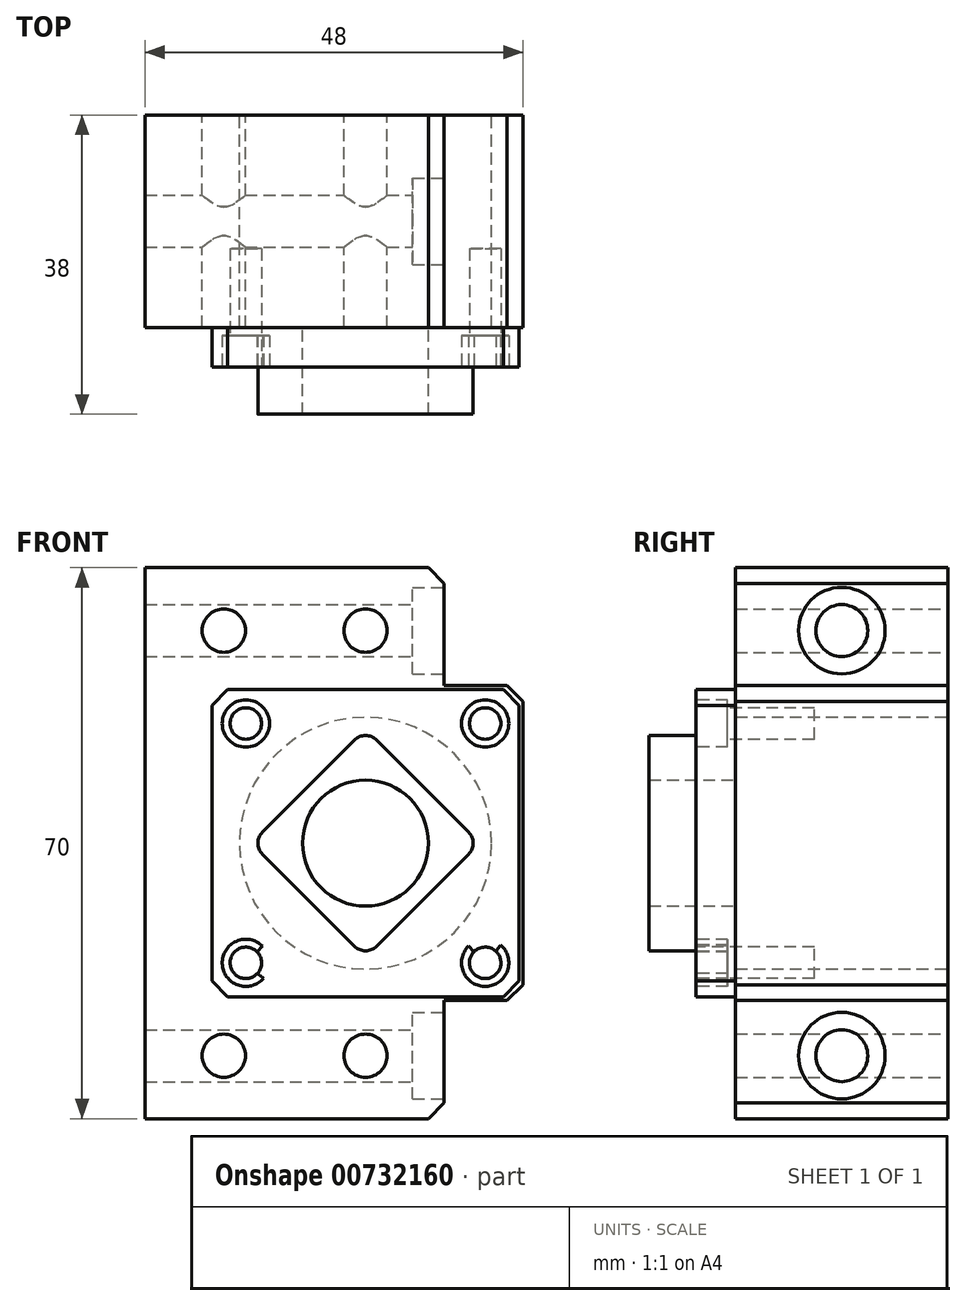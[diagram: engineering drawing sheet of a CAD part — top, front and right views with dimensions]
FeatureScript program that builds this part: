
annotation { "Feature Type Name" : "Feature", "Feature Type Description" : "" }
export const myFeature = defineFeature(function(context is Context, id is Id, definition is map)
    precondition{}
    {
        {
            var Q0;
            Q0=qCreatedBy(makeId("Front.planeOp"),FACE);
            var sketch = newSketch(context, id + "F0", { "sketchPlane" : qUnion([Q0])});
            skLineSegment(sketch, "E0.bottom", {"start": v(0, 0) * mm, "end": v(38, 0) * mm});
            skLineSegment(sketch, "E0.top", {"start": v(0, 70) * mm, "end": v(38, 70) * mm});
            skLineSegment(sketch, "E0.left", {"start": v(0, 0) * mm, "end": v(0, 70) * mm});
            skLineSegment(sketch, "E0.right", {"start": v(48, 15) * mm, "end": v(48, 55) * mm});
            skCircle(sketch, "E1", {"center": v(28, 35) * mm, "radius": 16 * mm});
            skCircle(sketch, "E2", {"center": v(10, 62) * mm, "radius": 2.75 * mm});
            skCircle(sketch, "E3", {"center": v(28, 62) * mm, "radius": 2.75 * mm});
            skCircle(sketch, "E4", {"center": v(10, 8) * mm, "radius": 2.75 * mm});
            skCircle(sketch, "E5", {"center": v(28, 8) * mm, "radius": 2.75 * mm});
            skLineSegment(sketch, "E6.top", {"start": v(48, 55) * mm, "end": v(38, 55) * mm});
            skLineSegment(sketch, "E6.right", {"start": v(38, 70) * mm, "end": v(38, 55) * mm});
            skLineSegment(sketch, "E7.top", {"start": v(48, 15) * mm, "end": v(38, 15) * mm});
            skLineSegment(sketch, "E7.right", {"start": v(38, 0) * mm, "end": v(38, 15) * mm});
            skPoint(sketch, "E6.bottom.start.orphan", {"position": v(48, 70) * mm});
            skSolve(sketch);
        }
        {
            var Q0;
            Q0=makeQuery(id+"F0.imprint","IMPRINT",FACE,{"disambiguationData":[TD([[makeQuery(id+"F0.imprint","IMPRINT",EDGE,{"derivedFrom":sQuery(id+"F0.wireOp",EDGE,"E0.bottom")}),1.0]])]});
            extrude(context, id + "F1", {"entities" : qUnion([Q0]), "depth" : 27 * mm, "offsetDistance" : 25 * mm});
        }
        {
            var Q0;
            Q0=makeQuery(id+"F1.opExtrude","SWEPT_FACE",FACE,{"disambiguationData":[OSD([sQuery(id+"F0.wireOp",EDGE,"E6.right")])]});
            var sketch = newSketch(context, id + "F2", { "sketchPlane" : qUnion([Q0])});
            skCircle(sketch, "E8", {"center": v(-13.5, 62) * mm, "radius": 3.3 * mm});
            skPoint(sketch, "E8.centerSnap0", {"position": v(-22.98, 62) * mm});
            skCircle(sketch, "E9", {"center": v(-13.5, 8) * mm, "radius": 3.3 * mm});
            skSolve(sketch);
        }
        {
            var Q0;
            Q0=qSketchRegion(id+"F2",true);
            extrude(context, id + "F3", {"entities" : qUnion([Q0]), "operationType" : NewBodyOperationType.REMOVE, "oppositeDirection" : true, "depth" : 38 * mm, "offsetDistance" : 25 * mm});
        }
        {
            var Q0;
            Q0=makeQuery(id+"F1.opExtrude","SWEPT_FACE",FACE,{"disambiguationData":[OSD([sQuery(id+"F0.wireOp",EDGE,"E6.right")])]});
            var sketch = newSketch(context, id + "F4", { "sketchPlane" : qUnion([Q0])});
            skCircle(sketch, "E10", {"center": v(-13.5, 62) * mm, "radius": 5.5 * mm});
            skCircle(sketch, "E11", {"center": v(-13.5, 8) * mm, "radius": 5.5 * mm});
            skSolve(sketch);
        }
        {
            var Q0;
            Q0=qSketchRegion(id+"F4",true);
            extrude(context, id + "F5", {"entities" : qUnion([Q0]), "operationType" : NewBodyOperationType.REMOVE, "oppositeDirection" : true, "depth" : 4 * mm, "offsetDistance" : 25 * mm});
        }
        {
            var Q0;
            Q0=makeQuery(id+"F1.opExtrude","SWEPT_EDGE",EDGE,{"disambiguationData":[OSD([sQuery(id+"F0.wireOp",EDGE,"E0.top"),sQuery(id+"F0.wireOp",EDGE,"E6.right")])]});
            var Q1;
            Q1=makeQuery(id+"F1.opExtrude","SWEPT_EDGE",EDGE,{"disambiguationData":[OSD([sQuery(id+"F0.wireOp",EDGE,"E0.right"),sQuery(id+"F0.wireOp",EDGE,"E6.top")])]});
            var Q2;
            Q2=makeQuery(id+"F1.opExtrude","SWEPT_EDGE",EDGE,{"disambiguationData":[OSD([sQuery(id+"F0.wireOp",EDGE,"E0.bottom"),sQuery(id+"F0.wireOp",EDGE,"E7.right")])]});
            var Q3;
            Q3=makeQuery(id+"F1.opExtrude","SWEPT_EDGE",EDGE,{"disambiguationData":[OSD([sQuery(id+"F0.wireOp",EDGE,"E0.right"),sQuery(id+"F0.wireOp",EDGE,"E7.top")])]});
            chamfer(context, id + "F6", {"entities" : qUnion([Q0, Q1, Q2, Q3]), "width" : 2 * mm, "tangentPropagation" : true});
        }
        {
            var Q0;
            Q0=makeQuery(id+"F1.opExtrude","CAP_FACE",FACE,{"disambiguationData":[OSD([sQuery(id+"F0.wireOp",EDGE,"E0.bottom"),sQuery(id+"F0.wireOp",EDGE,"E0.top"),sQuery(id+"F0.wireOp",EDGE,"E0.left"),sQuery(id+"F0.wireOp",EDGE,"E0.right"),sQuery(id+"F0.wireOp",EDGE,"E1"),sQuery(id+"F0.wireOp",EDGE,"E2"),sQuery(id+"F0.wireOp",EDGE,"E3"),sQuery(id+"F0.wireOp",EDGE,"E4"),sQuery(id+"F0.wireOp",EDGE,"E5"),sQuery(id+"F0.wireOp",EDGE,"E6.top"),sQuery(id+"F0.wireOp",EDGE,"E6.right"),sQuery(id+"F0.wireOp",EDGE,"E7.top"),sQuery(id+"F0.wireOp",EDGE,"E7.right")])],"isStart":false});
            var sketch = newSketch(context, id + "F7", { "sketchPlane" : qUnion([Q0])});
            skLineSegment(sketch, "E12.bottom", {"start": v(8.5, 15.5) * mm, "end": v(47.5, 15.5) * mm});
            skLineSegment(sketch, "E12.top", {"start": v(8.5, 54.5) * mm, "end": v(47.5, 54.5) * mm});
            skLineSegment(sketch, "E12.left", {"start": v(8.5, 15.5) * mm, "end": v(8.5, 54.5) * mm});
            skLineSegment(sketch, "E12.right", {"start": v(47.5, 15.5) * mm, "end": v(47.5, 54.5) * mm});
            skCircle(sketch, "E13", {"center": v(28, 35) * mm, "radius": 8 * mm});
            skSolve(sketch);
        }
        {
            var Q0;
            {var subQ11=sQuery(id+"F7.wireOp",EDGE,"E12.left");Q0=makeQuery(id+"F7.imprint","IMPRINT",FACE,{"disambiguationData":[TD([[makeQuery(id+"F7.imprint","IMPRINT",EDGE,{"derivedFrom":subQ11}),-1.0]])]});}
            var Q1;
            {var subQ0=sQuery(id+"F7.wireOp",EDGE,"E12.right");var subQ1=sQuery(id+"F7.wireOp",EDGE,"E12.top");var subQ2=makeQuery(id+"F7.imprint","INTERSECT",VERTEX,{"derivedFrom":[subQ1,subQ0]});Q1=makeQuery(id+"F7.imprint","IMPRINT",FACE,{"disambiguationData":[TD([[makeQuery(id+"F7.imprint","IMPRINT",EDGE,{"disambiguationData":[TD([[subQ2,1.0]])],"derivedFrom":subQ1}),-1.0]])]});}
            var Q2;
            {var subQ0=sQuery(id+"F7.wireOp",EDGE,"E12.right");var subQ1=sQuery(id+"F7.wireOp",EDGE,"E12.bottom");var subQ2=makeQuery(id+"F7.imprint","INTERSECT",VERTEX,{"derivedFrom":[subQ1,subQ0]});Q2=makeQuery(id+"F7.imprint","IMPRINT",FACE,{"disambiguationData":[TD([[makeQuery(id+"F7.imprint","IMPRINT",EDGE,{"disambiguationData":[TD([[subQ2,1.0]])],"derivedFrom":subQ1}),1.0]])]});}
            var Q3;
            Q3=makeQuery(id+"F7.imprint","IMPRINT",FACE,{"disambiguationData":[TD([[makeQuery(id+"F7.imprint","IMPRINT",EDGE,{"derivedFrom":sQuery(id+"F7.wireOp",EDGE,"E13")}),-1.0]])]});
            extrude(context, id + "F8", {"entities" : qUnion([Q0, Q1, Q2, Q3]), "operationType" : NewBodyOperationType.ADD, "depth" : 5 * mm, "offsetDistance" : 25 * mm});
        }
        {
            var Q0;
            Q0=makeQuery(id+"F8.opExtrude","SWEPT_EDGE",EDGE,{"disambiguationData":[OSD([sQuery(id+"F7.wireOp",EDGE,"E12.bottom"),sQuery(id+"F7.wireOp",EDGE,"E12.left")])]});
            var Q1;
            Q1=makeQuery(id+"F8.opExtrude","SWEPT_EDGE",EDGE,{"disambiguationData":[OSD([sQuery(id+"F7.wireOp",EDGE,"E12.bottom"),sQuery(id+"F7.wireOp",EDGE,"E12.right")])]});
            var Q2;
            Q2=makeQuery(id+"F8.opExtrude","SWEPT_EDGE",EDGE,{"disambiguationData":[OSD([sQuery(id+"F7.wireOp",EDGE,"E12.top"),sQuery(id+"F7.wireOp",EDGE,"E12.left")])]});
            var Q3;
            Q3=makeQuery(id+"F8.opExtrude","SWEPT_EDGE",EDGE,{"disambiguationData":[OSD([sQuery(id+"F7.wireOp",EDGE,"E12.top"),sQuery(id+"F7.wireOp",EDGE,"E12.right")])]});
            chamfer(context, id + "F9", {"entities" : qUnion([Q0, Q1, Q2, Q3]), "width" : 2 * mm, "tangentPropagation" : true});
        }
        {
            var Q0;
            Q0=makeQuery(id+"F8.opExtrude","CAP_FACE",FACE,{"disambiguationData":[OSD([sQuery(id+"F7.wireOp",EDGE,"E12.bottom"),sQuery(id+"F7.wireOp",EDGE,"E12.top"),sQuery(id+"F7.wireOp",EDGE,"E12.left"),sQuery(id+"F7.wireOp",EDGE,"E12.right"),sQuery(id+"F7.wireOp",EDGE,"E13")])],"isStart":false});
            var sketch = newSketch(context, id + "F10", { "sketchPlane" : qUnion([Q0])});
            skCircle(sketch, "E14", {"center": v(28, 35) * mm, "radius": 21.5 * mm});
            skLineSegment(sketch, "E15", {"start": v(28, 35) * mm, "end": v(46.5, 53.5) * mm});
            skLineSegment(sketch, "E16", {"start": v(28, 35) * mm, "end": v(9.5, 16.5) * mm});
            skLineSegment(sketch, "E17", {"start": v(9.5, 16.5) * mm, "end": v(28, 35) * mm});
            skLineSegment(sketch, "E18", {"start": v(28, 35) * mm, "end": v(46.5, 16.5) * mm});
            skLineSegment(sketch, "E19", {"start": v(46.5, 16.5) * mm, "end": v(28, 35) * mm});
            skLineSegment(sketch, "E20", {"start": v(28, 35) * mm, "end": v(9.5, 53.5) * mm});
            skCircle(sketch, "E21", {"center": v(43.2, 50.2) * mm, "radius": 3 * mm});
            skCircle(sketch, "E22", {"center": v(43.2, 19.8) * mm, "radius": 3 * mm});
            skCircle(sketch, "E23", {"center": v(12.8, 19.8) * mm, "radius": 3 * mm});
            skCircle(sketch, "E24", {"center": v(12.8, 50.2) * mm, "radius": 3 * mm});
            skSolve(sketch);
        }
        {
            var Q0;
            {var subQ0=sQuery(id+"F10.wireOp",EDGE,"E15");var subQ1=sQuery(id+"F10.wireOp",EDGE,"E14");var subQ2=makeQuery(id+"F10.imprint","INTERSECT",VERTEX,{"derivedFrom":[subQ1,subQ0]});Q0=makeQuery(id+"F10.imprint","IMPRINT",FACE,{"disambiguationData":[TD([[makeQuery(id+"F10.imprint","IMPRINT",EDGE,{"disambiguationData":[TD([[subQ2,-1.0]])],"derivedFrom":subQ1}),-1.0]])]});}
            var Q1;
            {var subQ0=sQuery(id+"F10.wireOp",EDGE,"E15");var subQ1=sQuery(id+"F10.wireOp",EDGE,"E14");var subQ2=makeQuery(id+"F10.imprint","INTERSECT",VERTEX,{"derivedFrom":[subQ1,subQ0]});Q1=makeQuery(id+"F10.imprint","IMPRINT",FACE,{"disambiguationData":[TD([[makeQuery(id+"F10.imprint","IMPRINT",EDGE,{"disambiguationData":[TD([[subQ2,1.0]])],"derivedFrom":subQ1}),1.0]])]});}
            var Q2;
            {var subQ0=sQuery(id+"F10.wireOp",EDGE,"E15");var subQ1=sQuery(id+"F10.wireOp",EDGE,"E14");var subQ2=makeQuery(id+"F10.imprint","INTERSECT",VERTEX,{"derivedFrom":[subQ1,subQ0]});Q2=makeQuery(id+"F10.imprint","IMPRINT",FACE,{"disambiguationData":[TD([[makeQuery(id+"F10.imprint","IMPRINT",EDGE,{"disambiguationData":[TD([[subQ2,1.0]])],"derivedFrom":subQ1}),-1.0]])]});}
            var Q3;
            {var subQ0=sQuery(id+"F10.wireOp",EDGE,"E15");var subQ1=sQuery(id+"F10.wireOp",EDGE,"E14");var subQ2=makeQuery(id+"F10.imprint","INTERSECT",VERTEX,{"derivedFrom":[subQ1,subQ0]});Q3=makeQuery(id+"F10.imprint","IMPRINT",FACE,{"disambiguationData":[TD([[makeQuery(id+"F10.imprint","IMPRINT",EDGE,{"disambiguationData":[TD([[subQ2,-1.0]])],"derivedFrom":subQ1}),1.0]])]});}
            var Q4;
            {var subQ0=sQuery(id+"F10.wireOp",EDGE,"E19");var subQ1=sQuery(id+"F10.wireOp",EDGE,"E14");var subQ2=makeQuery(id+"F10.imprint","INTERSECT",VERTEX,{"derivedFrom":[subQ1,subQ0]});Q4=makeQuery(id+"F10.imprint","IMPRINT",FACE,{"disambiguationData":[TD([[makeQuery(id+"F10.imprint","IMPRINT",EDGE,{"disambiguationData":[TD([[subQ2,-1.0]])],"derivedFrom":subQ1}),1.0]])]});}
            var Q5;
            {var subQ0=sQuery(id+"F10.wireOp",EDGE,"E19");var subQ1=sQuery(id+"F10.wireOp",EDGE,"E14");var subQ2=makeQuery(id+"F10.imprint","INTERSECT",VERTEX,{"derivedFrom":[subQ1,subQ0]});Q5=makeQuery(id+"F10.imprint","IMPRINT",FACE,{"disambiguationData":[TD([[makeQuery(id+"F10.imprint","IMPRINT",EDGE,{"disambiguationData":[TD([[subQ2,-1.0]])],"derivedFrom":subQ1}),-1.0]])]});}
            var Q6;
            {var subQ0=sQuery(id+"F10.wireOp",EDGE,"E22");var subQ1=sQuery(id+"F10.wireOp",EDGE,"E14");var subQ2=makeQuery(id+"F10.imprint","INTERSECT",VERTEX,{"disambiguationData":[OD(0.0)],"derivedFrom":[subQ1,subQ0]});Q6=makeQuery(id+"F10.imprint","IMPRINT",FACE,{"disambiguationData":[TD([[makeQuery(id+"F10.imprint","IMPRINT",EDGE,{"disambiguationData":[TD([[subQ2,-1.0]])],"derivedFrom":subQ1}),-1.0]])]});}
            var Q7;
            {var subQ0=sQuery(id+"F10.wireOp",EDGE,"E22");var subQ1=sQuery(id+"F10.wireOp",EDGE,"E14");var subQ2=makeQuery(id+"F10.imprint","INTERSECT",VERTEX,{"disambiguationData":[OD(0.0)],"derivedFrom":[subQ1,subQ0]});Q7=makeQuery(id+"F10.imprint","IMPRINT",FACE,{"disambiguationData":[TD([[makeQuery(id+"F10.imprint","IMPRINT",EDGE,{"disambiguationData":[TD([[subQ2,-1.0]])],"derivedFrom":subQ1}),1.0]])]});}
            var Q8;
            {var subQ0=sQuery(id+"F10.wireOp",EDGE,"E17");var subQ1=sQuery(id+"F10.wireOp",EDGE,"E14");var subQ2=makeQuery(id+"F10.imprint","INTERSECT",VERTEX,{"derivedFrom":[subQ1,subQ0]});Q8=makeQuery(id+"F10.imprint","IMPRINT",FACE,{"disambiguationData":[TD([[makeQuery(id+"F10.imprint","IMPRINT",EDGE,{"disambiguationData":[TD([[subQ2,-1.0]])],"derivedFrom":subQ1}),1.0]])]});}
            var Q9;
            {var subQ0=sQuery(id+"F10.wireOp",EDGE,"E23");var subQ1=sQuery(id+"F10.wireOp",EDGE,"E14");var subQ2=makeQuery(id+"F10.imprint","INTERSECT",VERTEX,{"disambiguationData":[OD(0.0)],"derivedFrom":[subQ1,subQ0]});Q9=makeQuery(id+"F10.imprint","IMPRINT",FACE,{"disambiguationData":[TD([[makeQuery(id+"F10.imprint","IMPRINT",EDGE,{"disambiguationData":[TD([[subQ2,-1.0]])],"derivedFrom":subQ1}),-1.0]])]});}
            var Q10;
            {var subQ0=sQuery(id+"F10.wireOp",EDGE,"E23");var subQ1=sQuery(id+"F10.wireOp",EDGE,"E14");var subQ2=makeQuery(id+"F10.imprint","INTERSECT",VERTEX,{"disambiguationData":[OD(0.0)],"derivedFrom":[subQ1,subQ0]});Q10=makeQuery(id+"F10.imprint","IMPRINT",FACE,{"disambiguationData":[TD([[makeQuery(id+"F10.imprint","IMPRINT",EDGE,{"disambiguationData":[TD([[subQ2,-1.0]])],"derivedFrom":subQ1}),1.0]])]});}
            var Q11;
            {var subQ0=sQuery(id+"F10.wireOp",EDGE,"E17");var subQ1=sQuery(id+"F10.wireOp",EDGE,"E14");var subQ2=makeQuery(id+"F10.imprint","INTERSECT",VERTEX,{"derivedFrom":[subQ1,subQ0]});Q11=makeQuery(id+"F10.imprint","IMPRINT",FACE,{"disambiguationData":[TD([[makeQuery(id+"F10.imprint","IMPRINT",EDGE,{"disambiguationData":[TD([[subQ2,-1.0]])],"derivedFrom":subQ1}),-1.0]])]});}
            var Q12;
            {var subQ0=sQuery(id+"F10.wireOp",EDGE,"E24");var subQ1=sQuery(id+"F10.wireOp",EDGE,"E14");var subQ2=makeQuery(id+"F10.imprint","INTERSECT",VERTEX,{"disambiguationData":[OD(0.0)],"derivedFrom":[subQ1,subQ0]});Q12=makeQuery(id+"F10.imprint","IMPRINT",FACE,{"disambiguationData":[TD([[makeQuery(id+"F10.imprint","IMPRINT",EDGE,{"disambiguationData":[TD([[subQ2,-1.0]])],"derivedFrom":subQ1}),-1.0]])]});}
            var Q13;
            {var subQ0=sQuery(id+"F10.wireOp",EDGE,"E20");var subQ1=sQuery(id+"F10.wireOp",EDGE,"E14");var subQ2=makeQuery(id+"F10.imprint","INTERSECT",VERTEX,{"derivedFrom":[subQ1,subQ0]});Q13=makeQuery(id+"F10.imprint","IMPRINT",FACE,{"disambiguationData":[TD([[makeQuery(id+"F10.imprint","IMPRINT",EDGE,{"disambiguationData":[TD([[subQ2,-1.0]])],"derivedFrom":subQ1}),1.0]])]});}
            var Q14;
            {var subQ0=sQuery(id+"F10.wireOp",EDGE,"E24");var subQ1=sQuery(id+"F10.wireOp",EDGE,"E14");var subQ2=makeQuery(id+"F10.imprint","INTERSECT",VERTEX,{"disambiguationData":[OD(0.0)],"derivedFrom":[subQ1,subQ0]});Q14=makeQuery(id+"F10.imprint","IMPRINT",FACE,{"disambiguationData":[TD([[makeQuery(id+"F10.imprint","IMPRINT",EDGE,{"disambiguationData":[TD([[subQ2,-1.0]])],"derivedFrom":subQ1}),1.0]])]});}
            var Q15;
            {var subQ0=sQuery(id+"F10.wireOp",EDGE,"E20");var subQ1=sQuery(id+"F10.wireOp",EDGE,"E14");var subQ2=makeQuery(id+"F10.imprint","INTERSECT",VERTEX,{"derivedFrom":[subQ1,subQ0]});Q15=makeQuery(id+"F10.imprint","IMPRINT",FACE,{"disambiguationData":[TD([[makeQuery(id+"F10.imprint","IMPRINT",EDGE,{"disambiguationData":[TD([[subQ2,-1.0]])],"derivedFrom":subQ1}),-1.0]])]});}
            extrude(context, id + "F11", {"entities" : qUnion([Q0, Q1, Q2, Q3, Q4, Q5, Q6, Q7, Q8, Q9, Q10, Q11, Q12, Q13, Q14, Q15]), "operationType" : NewBodyOperationType.REMOVE, "oppositeDirection" : true, "depth" : 4 * mm, "offsetDistance" : 25 * mm});
        }
        {
            var Q0;
            Q0=makeQuery(id+"F8.opExtrude","CAP_FACE",FACE,{"disambiguationData":[OSD([sQuery(id+"F7.wireOp",EDGE,"E12.bottom"),sQuery(id+"F7.wireOp",EDGE,"E12.top"),sQuery(id+"F7.wireOp",EDGE,"E12.left"),sQuery(id+"F7.wireOp",EDGE,"E12.right"),sQuery(id+"F7.wireOp",EDGE,"E13")])],"isStart":false});
            var sketch = newSketch(context, id + "F12", { "sketchPlane" : qUnion([Q0])});
            skCircle(sketch, "E25", {"center": v(43.2, 50.2) * mm, "radius": 2 * mm});
            skCircle(sketch, "E26", {"center": v(43.2, 19.8) * mm, "radius": 2 * mm});
            skCircle(sketch, "E27", {"center": v(12.8, 19.8) * mm, "radius": 2 * mm});
            skCircle(sketch, "E28", {"center": v(12.8, 50.2) * mm, "radius": 2 * mm});
            skSolve(sketch);
        }
        {
            var Q0;
            Q0=qSketchRegion(id+"F12",true);
            extrude(context, id + "F13", {"entities" : qUnion([Q0]), "operationType" : NewBodyOperationType.REMOVE, "oppositeDirection" : true, "depth" : 15 * mm, "offsetDistance" : 25 * mm});
        }
        {
            var Q0;
            Q0=makeQuery(id+"F8.opExtrude","CAP_FACE",FACE,{"disambiguationData":[OSD([sQuery(id+"F7.wireOp",EDGE,"E12.bottom"),sQuery(id+"F7.wireOp",EDGE,"E12.top"),sQuery(id+"F7.wireOp",EDGE,"E12.left"),sQuery(id+"F7.wireOp",EDGE,"E12.right"),sQuery(id+"F7.wireOp",EDGE,"E13")])],"isStart":false});
            var sketch = newSketch(context, id + "F14", { "sketchPlane" : qUnion([Q0])});
            skLineSegment(sketch, "E29", {"start": v(14.91, 36.41) * mm, "end": v(26.59, 48.09) * mm});
            skPoint(sketch, "E29.startSnap0", {"position": v(8.5, 35) * mm});
            skPoint(sketch, "E29.endSnap0", {"position": v(28, 54.5) * mm});
            skLineSegment(sketch, "E30", {"start": v(29.41, 48.09) * mm, "end": v(41.09, 36.41) * mm});
            skPoint(sketch, "E30.endSnap0", {"position": v(47.5, 35) * mm});
            skLineSegment(sketch, "E31", {"start": v(41.09, 33.59) * mm, "end": v(29.41, 21.91) * mm});
            skPoint(sketch, "E31.endSnap0", {"position": v(28, 15.5) * mm});
            skLineSegment(sketch, "E32", {"start": v(26.59, 21.91) * mm, "end": v(14.91, 33.59) * mm});
            skPoint(sketch, "E33.visualSharp", {"position": v(13.5, 35) * mm});
            skArc(sketch, "E33.filletArc", {"start": v(14.91, 36.41) * mm, "mid": v(14.33, 35) * mm, "end": v(14.91, 33.59) * mm});
            skPoint(sketch, "E34.visualSharp", {"position": v(28, 20.5) * mm});
            skArc(sketch, "E34.filletArc", {"start": v(26.59, 21.91) * mm, "mid": v(28, 21.33) * mm, "end": v(29.41, 21.91) * mm});
            skPoint(sketch, "E35.visualSharp", {"position": v(28, 49.5) * mm});
            skArc(sketch, "E35.filletArc", {"start": v(29.41, 48.09) * mm, "mid": v(28, 48.67) * mm, "end": v(26.59, 48.09) * mm});
            skPoint(sketch, "E36.visualSharp", {"position": v(42.5, 35) * mm});
            skArc(sketch, "E36.filletArc", {"start": v(41.09, 33.59) * mm, "mid": v(41.67, 35) * mm, "end": v(41.09, 36.41) * mm});
            skSolve(sketch);
        }
        {
            var Q0;
            Q0=makeQuery(id+"F14.imprint","IMPRINT",FACE,{"disambiguationData":[TD([[makeQuery(id+"F14.imprint","IMPRINT",EDGE,{"derivedFrom":sQuery(id+"F14.wireOp",EDGE,"E29")}),-1.0]])]});
            extrude(context, id + "F15", {"entities" : qUnion([Q0]), "operationType" : NewBodyOperationType.ADD, "depth" : 6 * mm, "offsetDistance" : 25 * mm});
        }
    });
